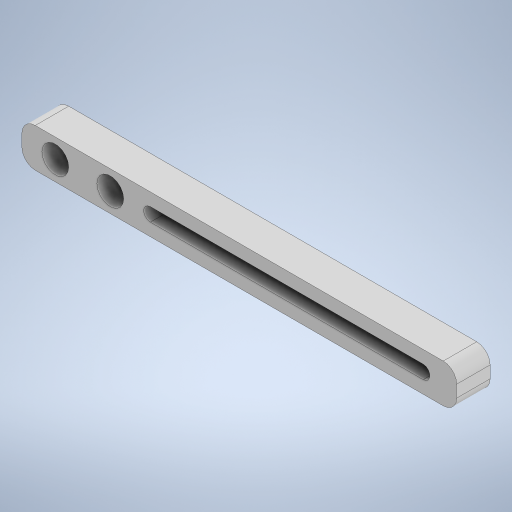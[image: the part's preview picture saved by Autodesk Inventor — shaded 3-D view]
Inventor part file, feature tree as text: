
AUTODESK INVENTOR PART (.ipt)
format: ipt  version: 2024 (Build 280153000, 153)  size: 283,648 bytes
history: native  units: mm
features: extrude x2, sketch x2, fillet x1, projected_geometry x1
ambient origin geometry x8: Origin, YZ Plane, XZ Plane, XY Plane, X Axis, Y Axis, Z Axis, Center Point
bodies: Solid1 (feature_tree)
feature tree (6):
  extrude  "Extrusion1"  Depth=5.8mm
  fillet  "Fillet1"  Radius=2.9mm
  extrude  "Extrusion2"  Depth=3.0mm
  sketch  "Sketch1"  dims[d0=65.0mm d1=5.8mm d2=2.9mm]
  sketch  "Sketch2"  dims[d3=5.0mm d4=8.217779mm d5=2.0mm d6=2.0mm d7=6.0mm d8=5.0mm d9=2.0mm d10=2.0mm d11=5.0mm d12=0.0mm d13=2.0mm d14=4.0mm d15=4.0mm d16=3.0mm d17=0.0mm]
  projected_geometry  "Projected Loop1"
